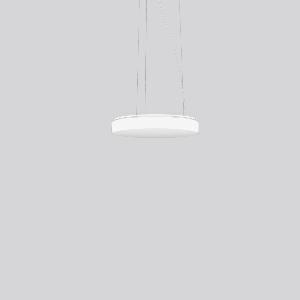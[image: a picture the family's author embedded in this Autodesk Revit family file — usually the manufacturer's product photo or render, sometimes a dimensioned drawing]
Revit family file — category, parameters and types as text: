
# Revit family: flat_polymero_kreis_slim_312089_002_2_76_d083
name_source: partatom
category: Lighting Fixtures
units: mm (PartAtom-declared; Revit-internal decimal feet)

## family parameters
Cut with Voids When Loaded = No
Host = Face
Light Source = No
Part Type = Normal
Room Calculation Point = No
Round Connector Dimension = Use Diameter
Shared = No

## types (1)
- FLAT POLYMERO KREIS SLIM (1 x LED Modul 830, 2000 lm, 3000)
    Apparent Load = 19 VA
    CIE Flux Codes = 43 74 93 89 100
    Color Rendering = 80
    Color Temperature = 3000
    Default Elevation = 1800 mm
    Description = Series: FLAT POLYMERO KREIS SLIM
Decorative round LED pendant luminaire. Base and canopy: metal, powder-coated, white. Canopy Ø 205 mm, h 35 mm. Diffuser made of plastic (polycarbonate), opal, shockproof. Diffuser fastening: patented push system. Homogeneous and smooth light distribution. Suitable for pendant. 3-point steel cable suspension, steplessly adjustable. Special lengths available on request. TouchDim sensor capable. Light and/or presence sensors can be integrated. 
Colour: white
Diameter: 360 mm
Height: 61 mm
Suspension length: 200-1300 mm
Lamp: LED
Socket: without socket
Colour temperature: 3000K
Colour rendering index (CRI): 83
System power: 19 W
Rated luminous flux: 2000 lm
Luminous efficiency: 105 lm/W
Control gear: AC power, DALI dimmable
Protection class: I
Type of protection: IP 40
    Height = 61 mm
    Lamp = 1 x LED Modul 830
    Lamp Light Flux = 2000 lm
    Lamp count = 1
    Length = 360 mm
    Lifetime = 50000 h
    Luminous efficacy = 105 lm/W
    Manufacturer = RZB
    ModVariant = No
    Model = 312089.002.2.76
    Mounting Place = Ceiling
    Mounting Type = Pendant
    Number of Poles = 1
    OnlyDefault = Yes
    Power Factor = 1
    Product Name = FLAT POLYMERO KREIS SLIM
    Product group = Pendant luminaires
    ProductGroupID = 902
    Protection Class = Protection class I
    Protection Degree = IP 40
    RLX_Detail_Level = 1
    RLX_Emergency_Light_Flux = 0 lm
    RLX_Emergency_Type = 0
    RLX_Emergency_Type_DB = No
    RlxData = <blob elided: 55997 chars, md5=cf832725>
    Socket = socket
    Standby Power = 0 W
    System Light Flux = 2000 lm
    System Power = 19 W
    Type Comments = Product without accessories
    Type Image = 312089.002.jpg
    URL = http://relux.com
    VarID = ---
    Voltage = 230 V
    Voltage Range = 220-240 V
    Weight = 0.00 kg
    Width = 0 mm  [stored 0 ft]

note: [stored X ft] marks values corroborated as IEEE doubles in the binary element streams (Revit-internal decimal feet)

## geometry (parser evidence)
native form markers: Blend x4, Sweep x15
no freeform markers — native parametric forms only
